# Revit family: Shower_Set-GROHE-New_Tempesta_Cosmopolitan_100-27578_Series
name_source: partatom
category: Plumbing Fixtures
revit_build: Autodesk Revit 2014 (Build: 20130308_1515(x64)
units: mm (PartAtom-declared; Revit-internal decimal feet)

## types (3) — shared parameters
ADA Compliant = Yes
Assembly Code = D2010710
CW Connection = Yes
CWFU = 3
Cold Water Connection Diameter = 1/2"
Cold Water Connection Radius = 1/4"
Default Elevation = 78"
Description = New Tempesta Cosmopolitan 100
Flow Rate = 2.0 gpm (7.6 L/min.)
HW Connection = Yes
HWFU = 3
Hot Water Connection Diameter = 1"
Hot Water Connection Radius = 1/4"
Installation Type = Wall Mounted
Length = 3 3/16"
Manufacturer = Grohe
Price = Prices may vary. Please consult Manufacturer Representative for most up-to-date price list.
Product Page URL = https://www.grohe.us
Tempered Connection Diameter = 1/2"
Tempered Connection Radius = 1/4"
URL = https://www.grohe.us
Vent Connection = No
WFU = 4
Warranty Documentation Link = https://cdn.cloud.grohe.com
Waste Connection = No
Width = 2 7/8"
cUPC Compliant = Yes

## per-type parameters (varying)
| type | Finish | Hand Shower Geometry | Height | Material | Type Comments |
| 27578000 | Metal-Grohe-000-Chrome | 27578 Shower Handle : 27578 Hand Shower 000 | 24 13/32" | Metal-Grohe-000-Chrome | *DISCONTINUED* |
| 2757810E | Metal-Grohe-10E-Chrome | 27578 Shower Handle : 27578 Hand Shower 10E | 24 7/16" | Metal-Grohe-10E-Chrome |  |
| 2757800E | Metal-Grohe-00E-Chrome | 27578 Shower Handle : 27578 Hand Shower 00E | 24 7/16" | Metal-Grohe-00E-Chrome |  |

note: column(s) folded — value = type name in every type: Model

## geometry (parser evidence)
native form markers: Sweep x6
no freeform markers — native parametric forms only
